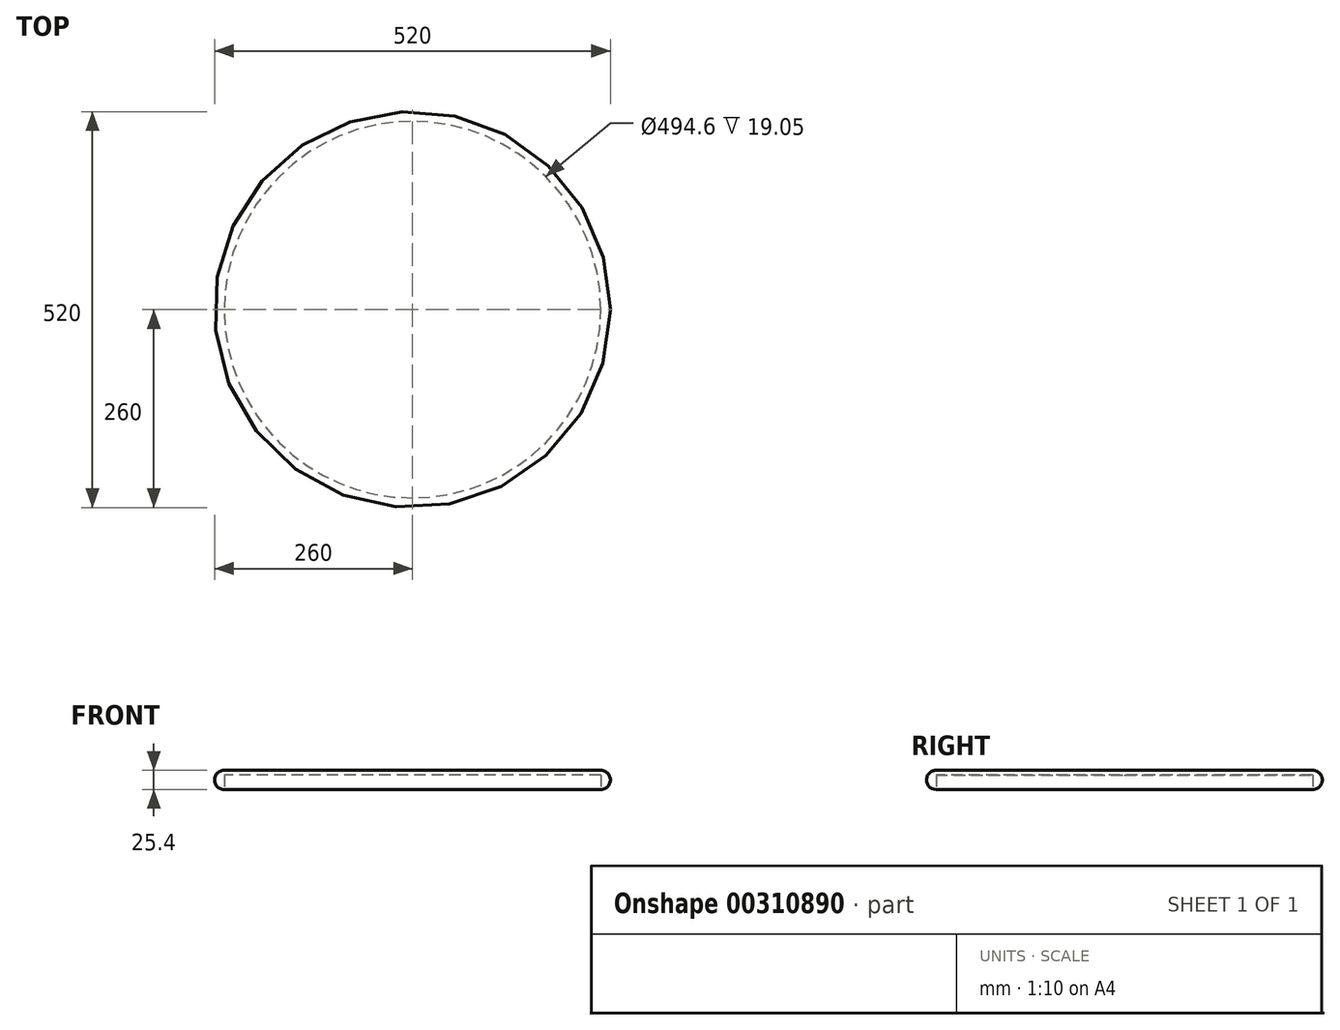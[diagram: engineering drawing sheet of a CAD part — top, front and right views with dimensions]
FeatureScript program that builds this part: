
annotation { "Feature Type Name" : "Feature", "Feature Type Description" : "" }
export const myFeature = defineFeature(function(context is Context, id is Id, definition is map)
    precondition{}
    {
        {
            var Q0;
            Q0=qCreatedBy(makeId("Top.planeOp"),FACE);
            var sketch = newSketch(context, id + "F0", { "sketchPlane" : qUnion([Q0])});
            skCircle(sketch, "E0", {"center": v(0, 0) * mm, "radius": 260 * mm});
            skSolve(sketch);
        }
        {
            var Q0;
            Q0=makeQuery(id+"F0.imprint","IMPRINT",FACE,{"disambiguationData":[TD([[makeQuery(id+"F0.imprint","IMPRINT",EDGE,{"derivedFrom":sQuery(id+"F0.wireOp",EDGE,"E0")}),1.0]])]});
            extrude(context, id + "F1", {"entities" : qUnion([Q0]), "depth" : 25.4 * mm});
        }
        {
            var Q0;
            Q0=makeQuery(id+"F1.opExtrude","CAP_FACE",FACE,{"disambiguationData":[OSD([sQuery(id+"F0.wireOp",EDGE,"E0")])],"isStart":false});
            var Q1;
            Q1=makeQuery(id+"F1.opExtrude","CAP_EDGE",EDGE,{"disambiguationData":[OSD([sQuery(id+"F0.wireOp",EDGE,"E0")])],"isStart":true});
            fillet(context, id + "F2", {"entities" : qUnion([Q0, Q1]), "radius" : 12.7 * mm, "tangentPropagation" : true, "allowEdgeOverflow" : false});
        }
        {
            var Q0;
            Q0=makeQuery(id+"F1.opExtrude","CAP_FACE",FACE,{"disambiguationData":[OSD([sQuery(id+"F0.wireOp",EDGE,"E0")])],"isStart":true});
            var sketch = newSketch(context, id + "F3", { "sketchPlane" : qUnion([Q0])});
            skCircle(sketch, "E1", {"center": v(-160.03, 166.03) * mm, "radius": 4 * mm});
            skCircle(sketch, "E2.MirrorC", {"center": v(160.03, 166.03) * mm, "radius": 4 * mm});
            skCircle(sketch, "E3.MirrorC", {"center": v(160.03, -166.03) * mm, "radius": 4 * mm});
            skCircle(sketch, "E4.MirrorC", {"center": v(-160.03, -166.03) * mm, "radius": 4 * mm});
            skSolve(sketch);
        }
        {
            var Q0;
            Q0=makeQuery(id+"F3.imprint","IMPRINT",FACE,{"disambiguationData":[TD([[makeQuery(id+"F3.imprint","IMPRINT",EDGE,{"derivedFrom":sQuery(id+"F3.wireOp",EDGE,"E2.MirrorC")}),-1.0]])]});
            extrude(context, id + "F4", {"entities" : qUnion([Q0]), "operationType" : NewBodyOperationType.REMOVE, "oppositeDirection" : true, "depth" : 19.05 * mm});
        }
        {
            var Q0;
            Q0 = qSketchRegion(id + "F3", true);
            extrude(context, id + "F5", {"entities" : qUnion([Q0]), "operationType" : NewBodyOperationType.REMOVE, "oppositeDirection" : true, "depth" : 19.05 * mm});
        }
    });
